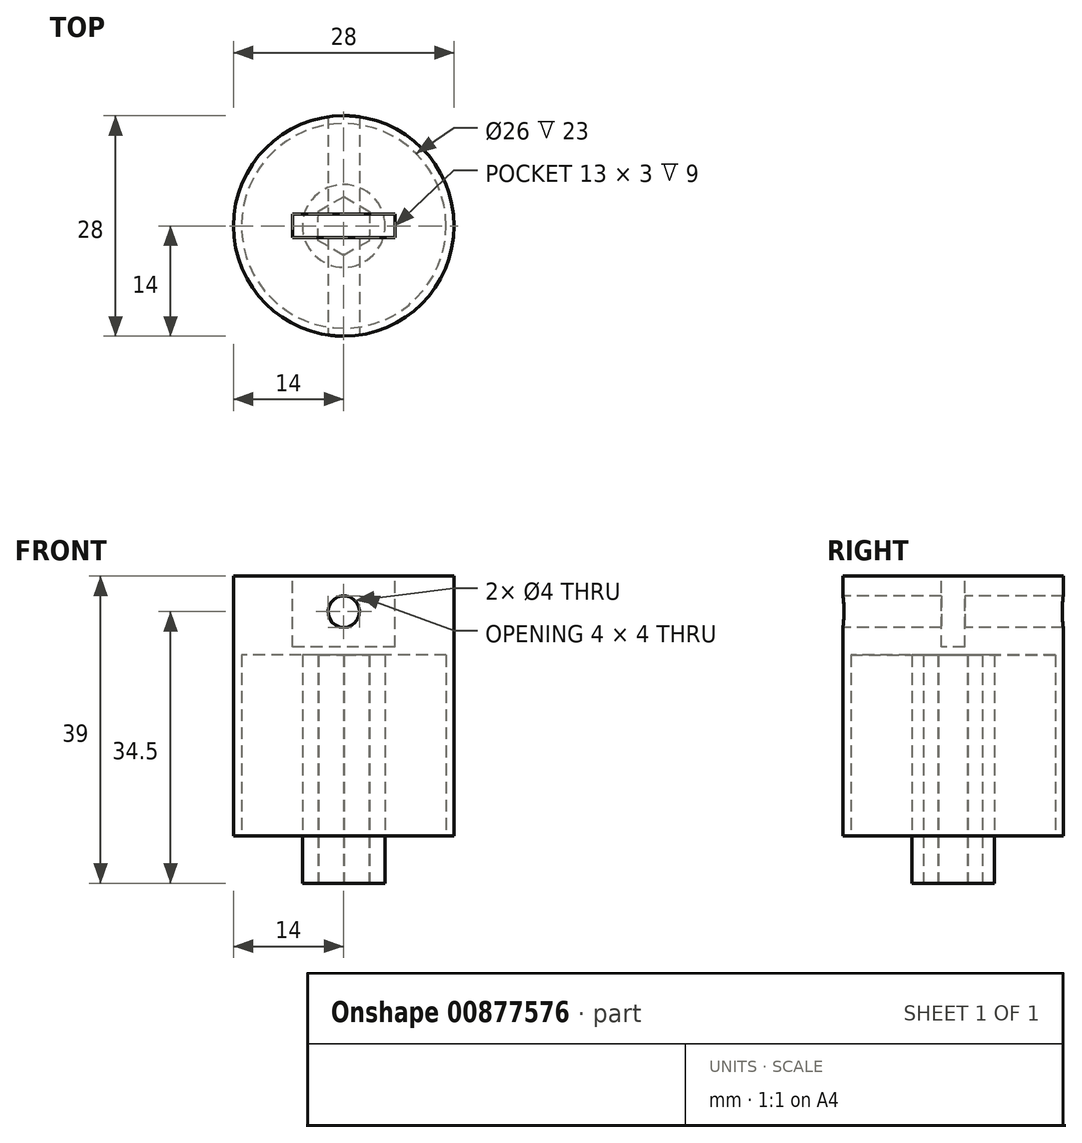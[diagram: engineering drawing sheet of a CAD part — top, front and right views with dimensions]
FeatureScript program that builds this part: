
annotation { "Feature Type Name" : "Feature", "Feature Type Description" : "" }
export const myFeature = defineFeature(function(context is Context, id is Id, definition is map)
    precondition{}
    {
        {
            var Q0;
            Q0=qCreatedBy(makeId("Top.planeOp"),FACE);
            var sketch = newSketch(context, id + "F0", { "sketchPlane" : qUnion([Q0])});
            skCircle(sketch, "E0.cCircle", {"center": v(0, 0) * mm, "radius": 3.25 * mm, "construction": true});
            skLineSegment(sketch, "E0.0", {"start": v(0.04, 3.75) * mm, "end": v(3.27, 1.84) * mm});
            skLineSegment(sketch, "E0.1", {"start": v(3.27, 1.84) * mm, "end": v(3.23, -1.91) * mm});
            skLineSegment(sketch, "E0.2", {"start": v(3.23, -1.91) * mm, "end": v(-0.04, -3.75) * mm});
            skLineSegment(sketch, "E0.3", {"start": v(-0.04, -3.75) * mm, "end": v(-3.27, -1.84) * mm});
            skLineSegment(sketch, "E0.4", {"start": v(-3.27, -1.84) * mm, "end": v(-3.23, 1.91) * mm});
            skLineSegment(sketch, "E0.5", {"start": v(-3.23, 1.91) * mm, "end": v(0.04, 3.75) * mm});
            skPoint(sketch, "E0.0.midPoint", {"position": v(1.65, 2.8) * mm});
            skCircle(sketch, "E1", {"center": v(0, 0) * mm, "radius": 5.25 * mm});
            skCircle(sketch, "E2", {"center": v(0, 0) * mm, "radius": 14 * mm});
            skCircle(sketch, "E3", {"center": v(0, 0) * mm, "radius": 13 * mm});
            skSolve(sketch);
        }
        {
            var Q0;
            Q0=makeQuery(id+"F0.imprint","IMPRINT",FACE,{"disambiguationData":[TD([[makeQuery(id+"F0.imprint","IMPRINT",EDGE,{"derivedFrom":sQuery(id+"F0.wireOp",EDGE,"E2")}),1.0]])]});
            var Q1;
            Q1=makeQuery(id+"F0.imprint","IMPRINT",FACE,{"disambiguationData":[TD([[makeQuery(id+"F0.imprint","IMPRINT",EDGE,{"derivedFrom":sQuery(id+"F0.wireOp",EDGE,"E0.0")}),1.0]])]});
            extrude(context, id + "F1", {"entities" : qUnion([Q0, Q1]), "depth" : 33 * mm, "offsetDistance" : 25 * mm});
        }
        {
            var Q0;
            Q0=makeQuery(id+"F0.imprint","IMPRINT",FACE,{"disambiguationData":[TD([[makeQuery(id+"F0.imprint","IMPRINT",EDGE,{"derivedFrom":sQuery(id+"F0.wireOp",EDGE,"E0.0")}),1.0]])]});
            extrude(context, id + "F2", {"entities" : qUnion([Q0]), "operationType" : NewBodyOperationType.ADD, "oppositeDirection" : true, "depth" : 6 * mm, "offsetDistance" : 25 * mm});
        }
        {
            var Q0;
            Q0=makeQuery(id+"F1.opExtrude","CAP_FACE",FACE,{"disambiguationData":[OSD([sQuery(id+"F0.wireOp",EDGE,"E0.0"),sQuery(id+"F0.wireOp",EDGE,"E0.1"),sQuery(id+"F0.wireOp",EDGE,"E0.2"),sQuery(id+"F0.wireOp",EDGE,"E0.3"),sQuery(id+"F0.wireOp",EDGE,"E0.4"),sQuery(id+"F0.wireOp",EDGE,"E0.5"),sQuery(id+"F0.wireOp",EDGE,"E1")])],"isStart":false});
            var sketch = newSketch(context, id + "F3", { "sketchPlane" : qUnion([Q0])});
            skCircle(sketch, "E4", {"center": v(0, 0) * mm, "radius": 14 * mm});
            skSolve(sketch);
        }
        {
            var Q0;
            Q0=makeQuery(id+"F3.imprint","IMPRINT",FACE,{"disambiguationData":[TD([[makeQuery(id+"F3.imprint","IMPRINT",EDGE,{"derivedFrom":sQuery(id+"F3.wireOp",EDGE,"E4")}),1.0]])]});
            var Q1;
            Q1=makeQuery(id+"F3.imprint","IMPRINT",FACE,{"disambiguationData":[TD([[makeQuery(id+"F3.imprint","IMPRINT",EDGE,{"derivedFrom":makeQuery(id+"F1.opExtrude","CAP_EDGE",EDGE,{"disambiguationData":[OSD([sQuery(id+"F0.wireOp",EDGE,"E0.0")])],"isStart":false})}),-1.0]])]});
            extrude(context, id + "F4", {"entities" : qUnion([Q0, Q1]), "oppositeDirection" : true, "depth" : 10 * mm, "offsetDistance" : 25 * mm});
        }
        {
            var Q0;
            Q0=makeQuery(id+"F1.opExtrude","SWEPT_BODY",BODY,{"disambiguationData":[OSD([sQuery(id+"F0.wireOp",EDGE,"E0.0"),sQuery(id+"F0.wireOp",EDGE,"E0.1"),sQuery(id+"F0.wireOp",EDGE,"E0.2"),sQuery(id+"F0.wireOp",EDGE,"E0.3"),sQuery(id+"F0.wireOp",EDGE,"E0.4"),sQuery(id+"F0.wireOp",EDGE,"E0.5"),sQuery(id+"F0.wireOp",EDGE,"E1")])]});
            var Q1;
            Q1=makeQuery(id+"F4.opExtrude","SWEPT_BODY",BODY,{"disambiguationData":[OSD([sQuery(id+"F3.wireOp",EDGE,"E4"),sQuery(id+"F3.wireOp",EDGE,"0khWDtHo-Dony-bPaE-VDFs-yVNV0XrjG9pL")])]});
            var Q2;
            Q2=makeQuery(id+"F1.opExtrude","SWEPT_BODY",BODY,{"disambiguationData":[OSD([sQuery(id+"F0.wireOp",EDGE,"E2"),sQuery(id+"F0.wireOp",EDGE,"E3")])]});
            booleanBodies(context, id + "F5", {"operationType" : BooleanOperationType.UNION, "tools" : qUnion([Q0, Q1, Q2])});
        }
        {
            var Q0;
            Q0=makeQuery(id+"F1.opExtrude","SWEPT_BODY",BODY,{"disambiguationData":[OSD([sQuery(id+"F0.wireOp",EDGE,"E0.0"),sQuery(id+"F0.wireOp",EDGE,"E0.1"),sQuery(id+"F0.wireOp",EDGE,"E0.2"),sQuery(id+"F0.wireOp",EDGE,"E0.3"),sQuery(id+"F0.wireOp",EDGE,"E0.4"),sQuery(id+"F0.wireOp",EDGE,"E0.5"),sQuery(id+"F0.wireOp",EDGE,"E1")])]});
            var Q1;
            Q1=makeQuery(id+"F4.opExtrude","SWEPT_BODY",BODY,{"disambiguationData":[OSD([sQuery(id+"F0.wireOp",EDGE,"E0.0"),sQuery(id+"F0.wireOp",EDGE,"E0.1"),sQuery(id+"F0.wireOp",EDGE,"E0.2"),sQuery(id+"F0.wireOp",EDGE,"E0.3"),sQuery(id+"F0.wireOp",EDGE,"E0.4"),sQuery(id+"F0.wireOp",EDGE,"E0.5")])]});
            booleanBodies(context, id + "F6", {"operationType" : BooleanOperationType.UNION, "tools" : qUnion([Q0, Q1])});
        }
        {
            var Q0;
            {var subQ0=sQuery(id+"F0.wireOp",EDGE,"E1");var subQ1=sQuery(id+"F0.wireOp",EDGE,"E0.5");var subQ2=sQuery(id+"F0.wireOp",EDGE,"E0.4");var subQ3=sQuery(id+"F0.wireOp",EDGE,"E0.3");var subQ4=sQuery(id+"F0.wireOp",EDGE,"E0.2");var subQ5=sQuery(id+"F0.wireOp",EDGE,"E0.1");var subQ6=sQuery(id+"F0.wireOp",EDGE,"E0.0");Q0=makeQuery(id+"F6.opBoolean","MERGE",FACE,{"derivedFrom":[makeQuery(id+"F4.opExtrude","CAP_FACE",FACE,{"disambiguationData":[OSD([subQ6,subQ5,subQ4,subQ3,subQ2,subQ1])],"isStart":true}),makeQuery(id+"F5.opBoolean","MERGE",FACE,{"derivedFrom":[makeQuery(id+"F1.opExtrude","CAP_FACE",FACE,{"disambiguationData":[OSD([subQ6,subQ5,subQ4,subQ3,subQ2,subQ1,subQ0])],"isStart":false}),makeQuery(id+"F4.opExtrude","CAP_FACE",FACE,{"disambiguationData":[OSD([subQ0,sQuery(id+"F3.wireOp",EDGE,"E4")])],"isStart":true})]})]});}
            var sketch = newSketch(context, id + "F7", { "sketchPlane" : qUnion([Q0])});
            skLineSegment(sketch, "E5.bottom", {"start": v(6.5, 1.5) * mm, "end": v(-6.5, 1.5) * mm});
            skLineSegment(sketch, "E5.top", {"start": v(6.5, -1.5) * mm, "end": v(-6.5, -1.5) * mm});
            skLineSegment(sketch, "E5.left", {"start": v(6.5, 1.5) * mm, "end": v(6.5, -1.5) * mm});
            skLineSegment(sketch, "E5.right", {"start": v(-6.5, 1.5) * mm, "end": v(-6.5, -1.5) * mm});
            skPoint(sketch, "E5.middle", {"position": v(0, 0) * mm});
            skSolve(sketch);
        }
        {
            var Q0;
            Q0=makeQuery(id+"F7.imprint","IMPRINT",FACE,{"disambiguationData":[TD([[makeQuery(id+"F7.imprint","IMPRINT",EDGE,{"derivedFrom":sQuery(id+"F7.wireOp",EDGE,"E5.bottom")}),1.0]])]});
            extrude(context, id + "F8", {"entities" : qUnion([Q0]), "operationType" : NewBodyOperationType.REMOVE, "oppositeDirection" : true, "depth" : 9 * mm, "offsetDistance" : 25 * mm});
        }
        {
            var Q0;
            Q0=makeQuery(id+"F8.boolean.opBoolean","COPY",FACE,{"derivedFrom":makeQuery(id+"F8.opExtrude","SWEPT_FACE",FACE,{"disambiguationData":[OSD([sQuery(id+"F7.wireOp",EDGE,"E5.bottom")])]})});
            var sketch = newSketch(context, id + "F9", { "sketchPlane" : qUnion([Q0])});
            skLineSegment(sketch, "E6", {"start": v(6.5, 33) * mm, "end": v(-6.5, 24) * mm, "construction": true});
            skLineSegment(sketch, "E7", {"start": v(-6.5, 33) * mm, "end": v(6.5, 24) * mm, "construction": true});
            skCircle(sketch, "E8", {"center": v(0, 28.5) * mm, "radius": 2 * mm});
            skSolve(sketch);
        }
        {
            var Q0;
            Q0=makeQuery(id+"F9.imprint","IMPRINT",FACE,{"disambiguationData":[TD([[makeQuery(id+"F9.imprint","IMPRINT",EDGE,{"derivedFrom":sQuery(id+"F9.wireOp",EDGE,"E8")}),1.0]])]});
            extrude(context, id + "F10", {"entities" : qUnion([Q0]), "operationType" : NewBodyOperationType.REMOVE, "endBound" : BoundingType.SYMMETRIC, "oppositeDirection" : true, "depth" : 32 * mm, "offsetDistance" : 25 * mm});
        }
    });
